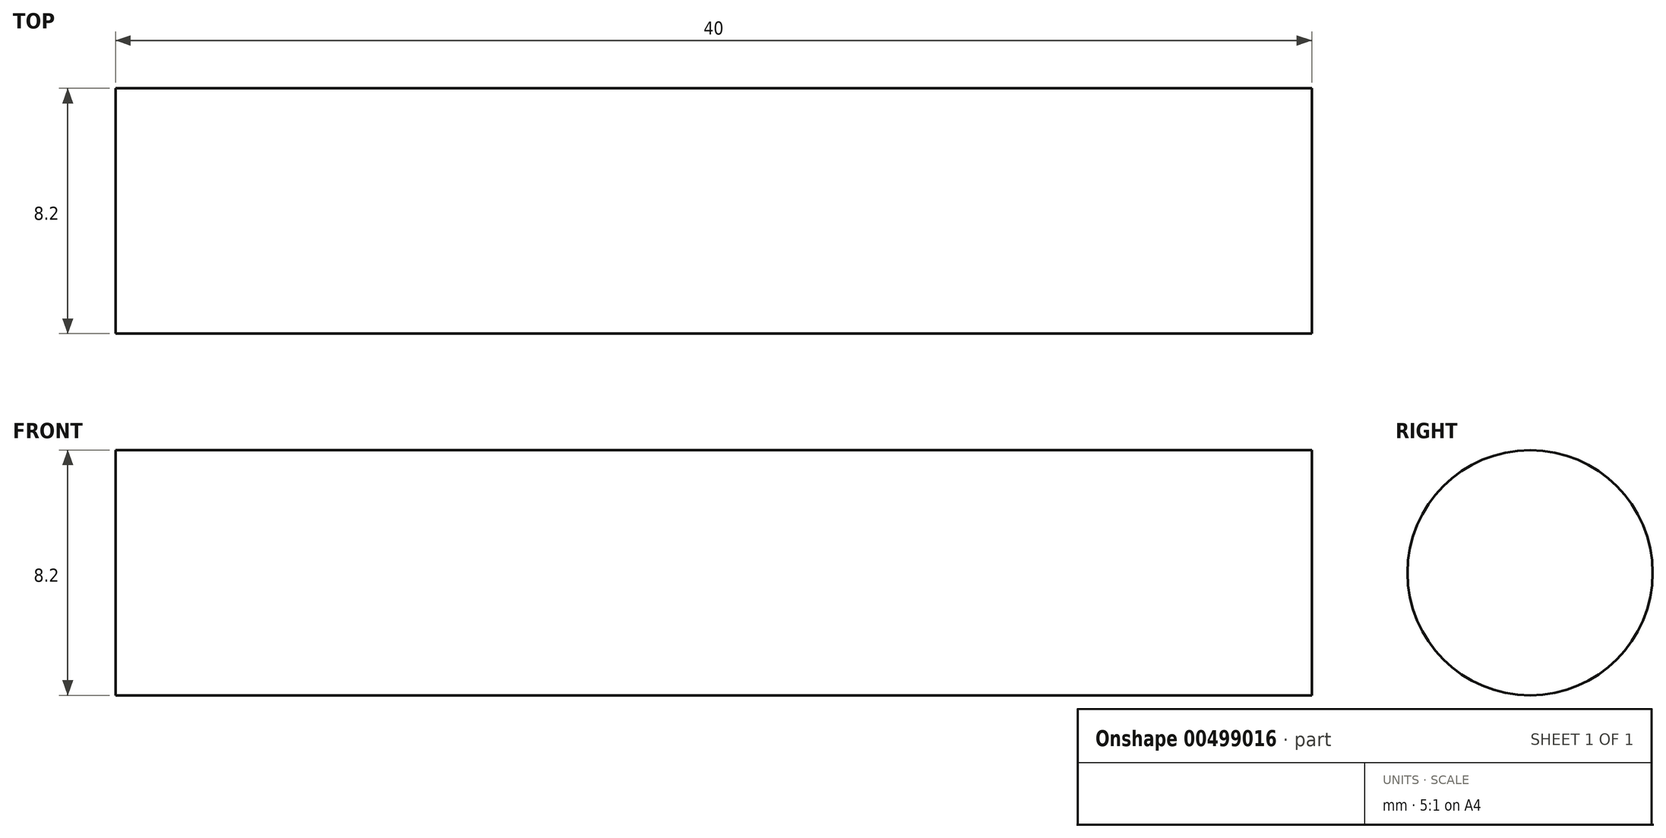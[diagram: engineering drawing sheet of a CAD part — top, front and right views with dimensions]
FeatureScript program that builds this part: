
annotation { "Feature Type Name" : "Feature", "Feature Type Description" : "" }
export const myFeature = defineFeature(function(context is Context, id is Id, definition is map)
    precondition{}
    {
        {
            var Q0;
            Q0=qCreatedBy(makeId("Right.planeOp"),FACE);
            var sketch = newSketch(context, id + "F0", { "sketchPlane" : qUnion([Q0])});
            skCircle(sketch, "E0", {"center": v(0, 0) * mm, "radius": 4.1 * mm});
            skSolve(sketch);
        }
        {
            var Q0;
            Q0=makeQuery(id+"F0.imprint","IMPRINT",FACE,{"disambiguationData":[TD([[makeQuery(id+"F0.imprint","IMPRINT",EDGE,{"derivedFrom":sQuery(id+"F0.wireOp",EDGE,"E0")}),1.0]])]});
            extrude(context, id + "F1", {"entities" : qUnion([Q0]), "endBound" : BoundingType.SYMMETRIC, "depth" : 40 * mm});
        }
    });
